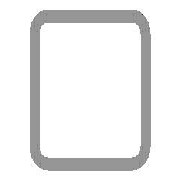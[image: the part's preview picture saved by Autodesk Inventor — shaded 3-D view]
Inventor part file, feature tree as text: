
AUTODESK INVENTOR PART (.ipt)
format: ipt  version: 2022 (Build 260153000, 153)  size: 136,704 bytes
history: native  units: mm (DEFAULTED — no unit token found)
features: other x4, sketch x3, plane x1
ambient origin geometry x8: Origin, YZ Plane, XZ Plane, XY Plane, X Axis, Y Axis, Z Axis, Center Point
bodies: Solid1 (feature_tree), Body (feature_tree)
feature tree (8):
  parser-record x1  (decoder bookkeeping rows leaked as tree rows — omitted from the tree; the rows remain in map.json)
  other  "Driven Length"
  other  "Start Plane"
  other  "End Plane"
  sketch  "Sketch"  dims[d7=7.5mm d10=40.0mm d11=40.0mm d12=5.0mm d13=-0.0mm d14=450.0mm d15=20.0mm d16=20.0mm d17=90.0deg d18=450.0mm]
  sketch  "Sketch3"  dims[d3=450.0mm]
  plane  "Work Plane3"
  sketch  "Sketch4"  dims[d4=0.0mm]
